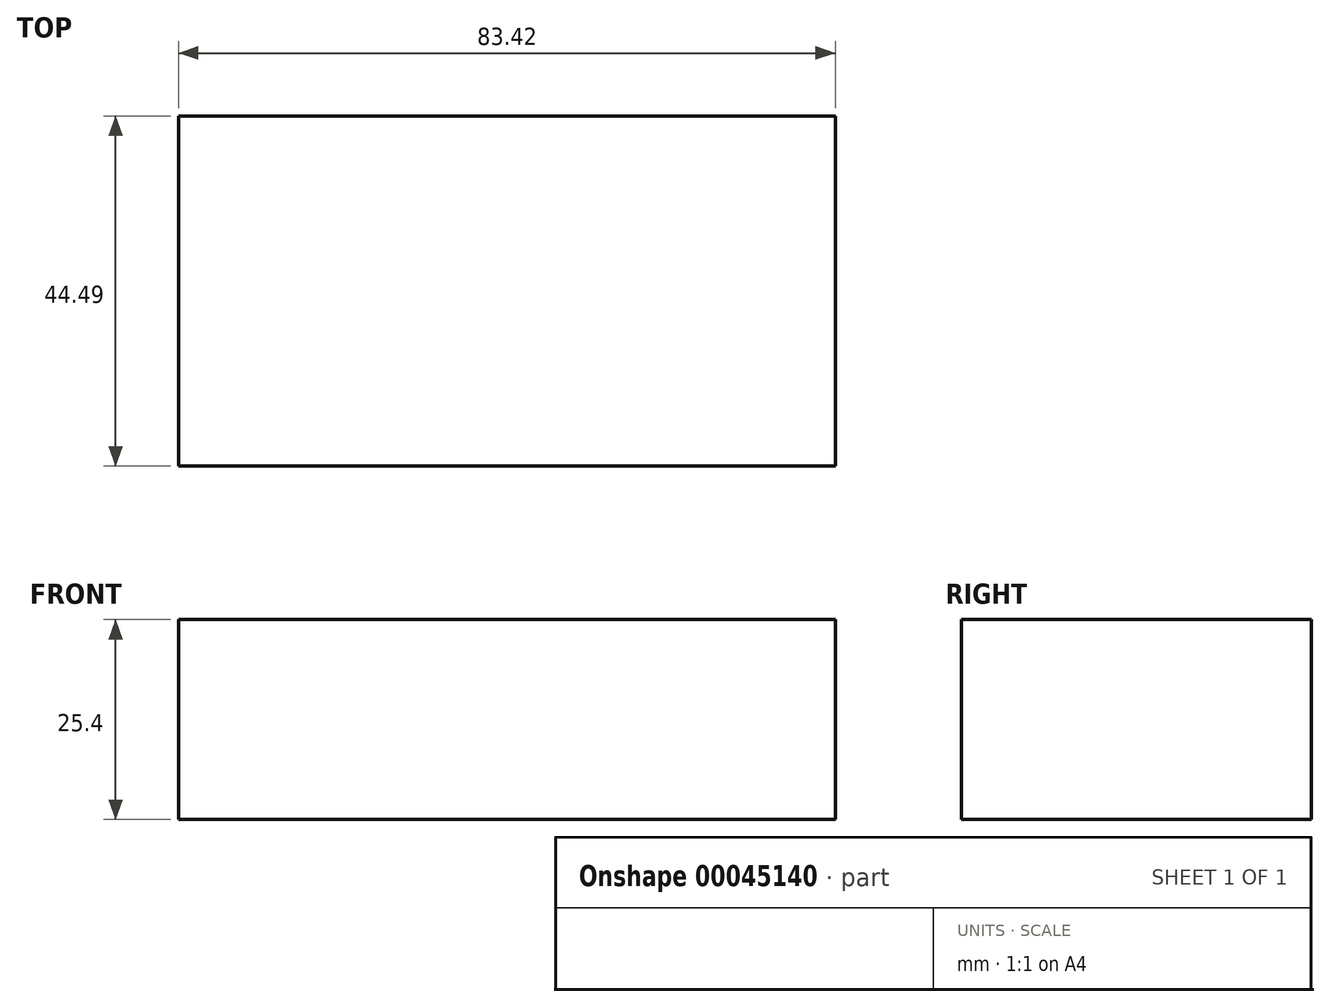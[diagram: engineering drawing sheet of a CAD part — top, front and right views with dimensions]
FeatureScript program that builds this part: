
annotation { "Feature Type Name" : "Feature", "Feature Type Description" : "" }
export const myFeature = defineFeature(function(context is Context, id is Id, definition is map)
    precondition{}
    {
        {
            var Q0;
            Q0=qCreatedBy(makeId("Top.planeOp"),FACE);
            var sketch = newSketch(context, id + "F0", { "sketchPlane" : qUnion([Q0])});
            skLineSegment(sketch, "E0.bottom", {"start": v(-36.87, 15.36) * mm, "end": v(46.55, 15.36) * mm});
            skLineSegment(sketch, "E0.top", {"start": v(-36.87, -29.13) * mm, "end": v(46.55, -29.13) * mm});
            skLineSegment(sketch, "E0.left", {"start": v(-36.87, 15.36) * mm, "end": v(-36.87, -29.13) * mm});
            skLineSegment(sketch, "E0.right", {"start": v(46.55, 15.36) * mm, "end": v(46.55, -29.13) * mm});
            skSolve(sketch);
        }
        {
            var Q0;
            Q0=makeQuery(id+"F0.imprint","IMPRINT",FACE,{"disambiguationData":[TD([[makeQuery(id+"F0.imprint","IMPRINT",EDGE,{"derivedFrom":sQuery(id+"F0.wireOp",EDGE,"E0.bottom")}),-1.0]])]});
            extrude(context, id + "F1", {"entities" : qUnion([Q0]), "depth" : 25.4 * mm});
        }
    });
